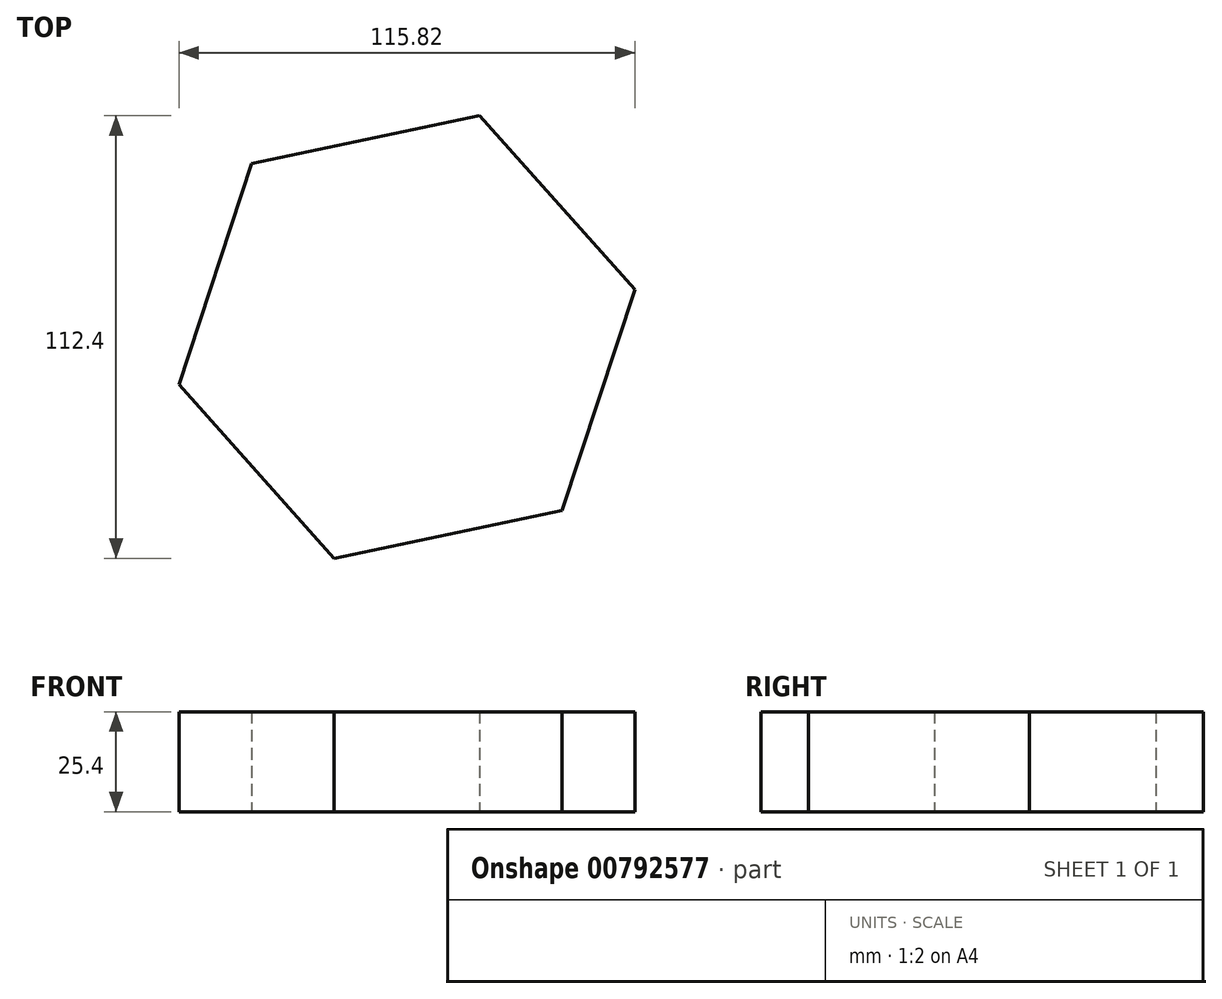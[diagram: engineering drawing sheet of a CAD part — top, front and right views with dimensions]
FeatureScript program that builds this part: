
annotation { "Feature Type Name" : "Feature", "Feature Type Description" : "" }
export const myFeature = defineFeature(function(context is Context, id is Id, definition is map)
    precondition{}
    {
        {
            var Q0;
            Q0=qCreatedBy(makeId("Top.planeOp"),FACE);
            var sketch = newSketch(context, id + "F0", { "sketchPlane" : qUnion([Q0])});
            skCircle(sketch, "E0.cCircle", {"center": v(0, 0) * mm, "radius": 51.24 * mm, "construction": true});
            skLineSegment(sketch, "E0.0", {"start": v(-39.43, 44.1) * mm, "end": v(18.48, 56.2) * mm});
            skLineSegment(sketch, "E0.1", {"start": v(18.48, 56.2) * mm, "end": v(57.91, 12.1) * mm});
            skLineSegment(sketch, "E0.2", {"start": v(57.91, 12.1) * mm, "end": v(39.43, -44.1) * mm});
            skLineSegment(sketch, "E0.3", {"start": v(39.43, -44.1) * mm, "end": v(-18.48, -56.2) * mm});
            skLineSegment(sketch, "E0.4", {"start": v(-18.48, -56.2) * mm, "end": v(-57.91, -12.1) * mm});
            skLineSegment(sketch, "E0.5", {"start": v(-57.91, -12.1) * mm, "end": v(-39.43, 44.1) * mm});
            skPoint(sketch, "E0.0.midPoint", {"position": v(-10.48, 50.15) * mm});
            skSolve(sketch);
        }
        {
            var Q0;
            Q0=makeQuery(id+"F0.imprint","IMPRINT",FACE,{"disambiguationData":[TD([[makeQuery(id+"F0.imprint","IMPRINT",EDGE,{"derivedFrom":sQuery(id+"F0.wireOp",EDGE,"E0.0")}),-1.0]])]});
            extrude(context, id + "F1", {"entities" : qUnion([Q0]), "depth" : 25.4 * mm, "offsetDistance" : 25.4 * mm});
        }
    });
